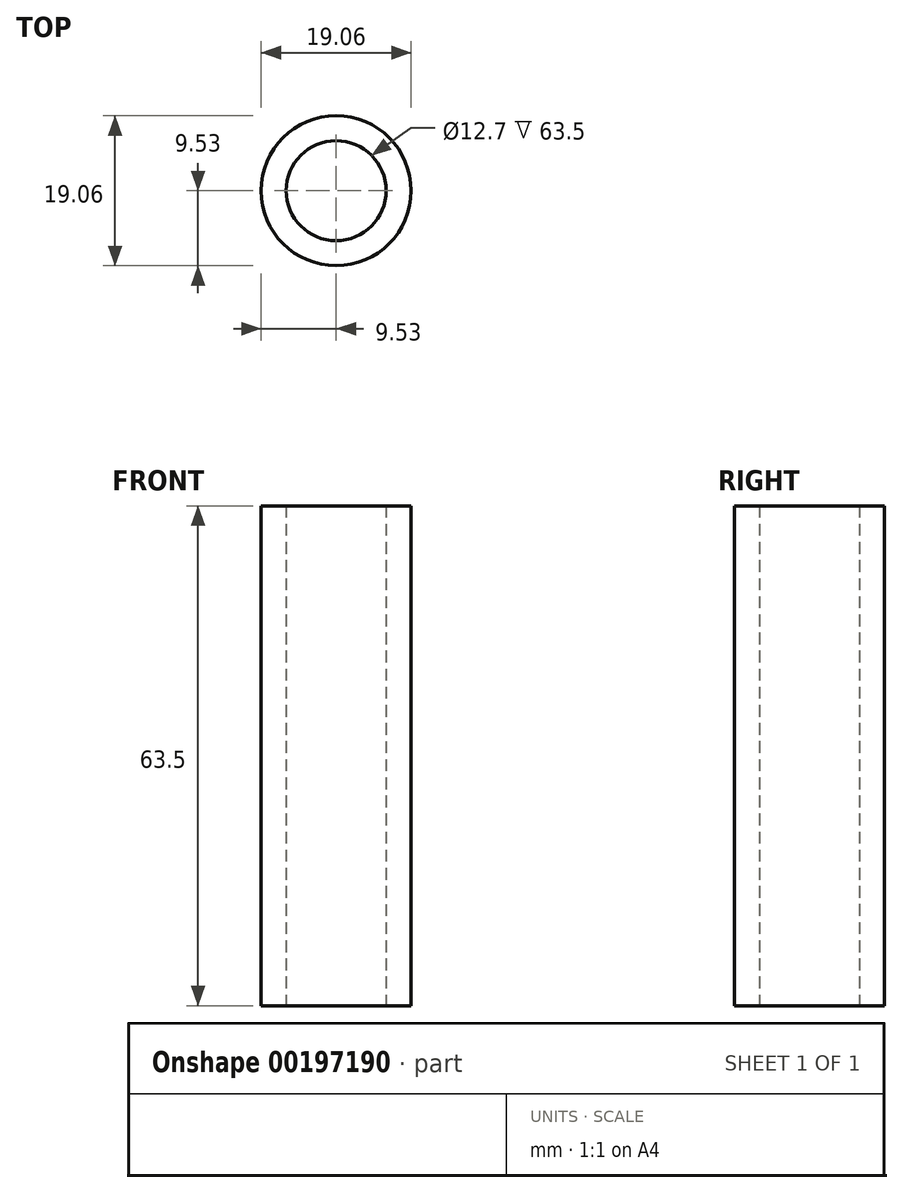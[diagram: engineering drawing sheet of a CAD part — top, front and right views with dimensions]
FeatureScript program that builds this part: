
annotation { "Feature Type Name" : "Feature", "Feature Type Description" : "" }
export const myFeature = defineFeature(function(context is Context, id is Id, definition is map)
    precondition{}
    {
        {
            var Q0;
            Q0=qCreatedBy(makeId("Top.planeOp"),FACE);
            var sketch = newSketch(context, id + "F0", { "sketchPlane" : qUnion([Q0])});
            skCircle(sketch, "E0", {"center": v(0, 0) * mm, "radius": 9.53 * mm});
            skCircle(sketch, "E1", {"center": v(0, 0) * mm, "radius": 6.35 * mm});
            skSolve(sketch);
        }
        {
            var Q0;
            Q0=makeQuery(id+"F0.imprint","IMPRINT",FACE,{"disambiguationData":[TD([[makeQuery(id+"F0.imprint","IMPRINT",EDGE,{"derivedFrom":sQuery(id+"F0.wireOp",EDGE,"E0")}),1.0]])]});
            extrude(context, id + "F1", {"entities" : qUnion([Q0]), "depth" : 63.5 * mm});
        }
    });
